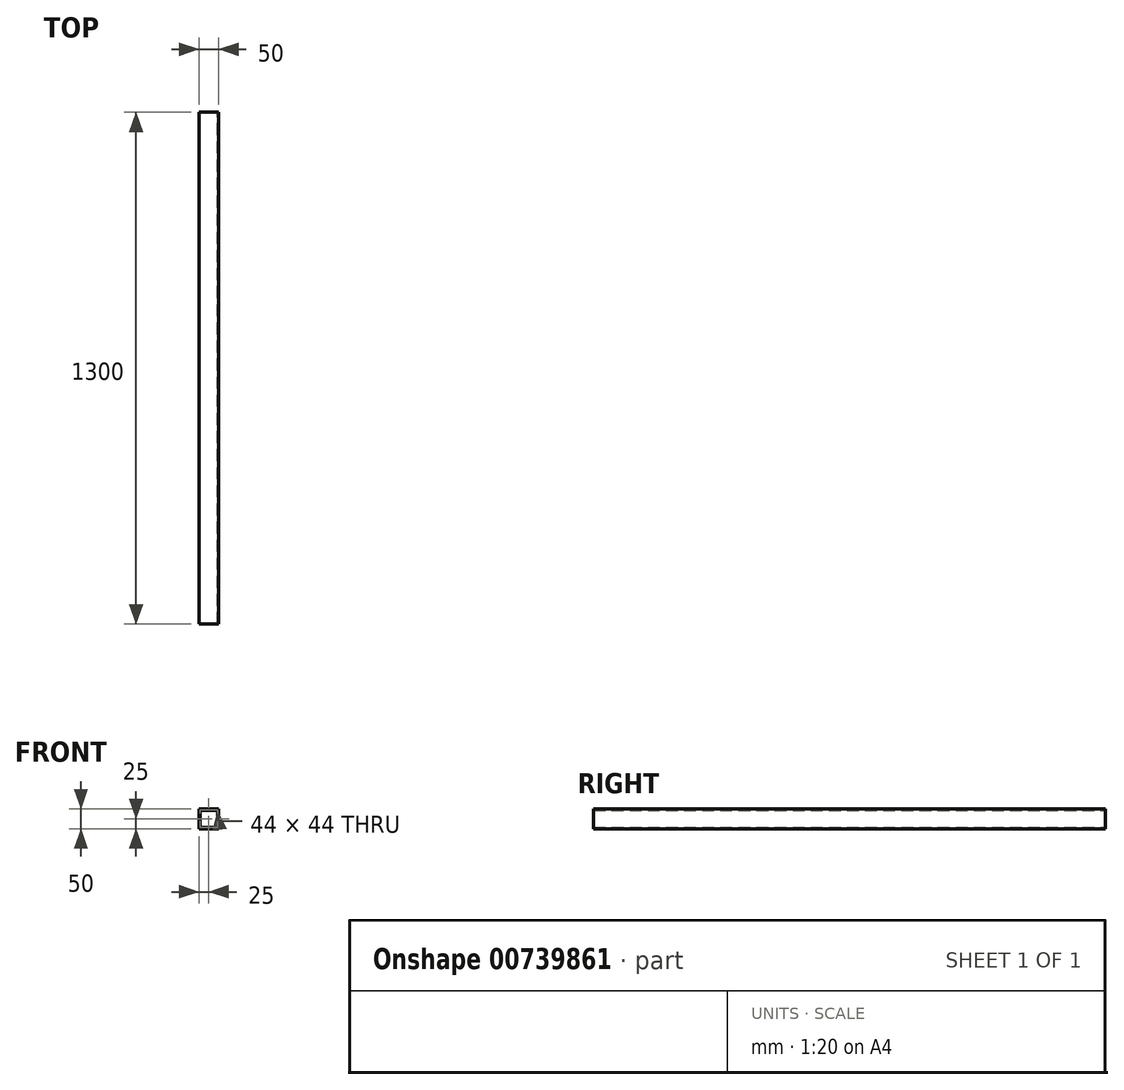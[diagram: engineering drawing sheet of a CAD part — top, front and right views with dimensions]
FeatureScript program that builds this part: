
annotation { "Feature Type Name" : "Feature", "Feature Type Description" : "" }
export const myFeature = defineFeature(function(context is Context, id is Id, definition is map)
    precondition{}
    {
        {
            var Q0;
            Q0=qCreatedBy(makeId("Front.planeOp"),FACE);
            var sketch = newSketch(context, id + "F0", { "sketchPlane" : qUnion([Q0])});
            skLineSegment(sketch, "E0.bottom", {"start": v(25, -25) * mm, "end": v(-25, -25) * mm});
            skLineSegment(sketch, "E0.top", {"start": v(25, 25) * mm, "end": v(-25, 25) * mm});
            skLineSegment(sketch, "E0.left", {"start": v(25, -25) * mm, "end": v(25, 25) * mm});
            skLineSegment(sketch, "E0.right", {"start": v(-25, -25) * mm, "end": v(-25, 25) * mm});
            skPoint(sketch, "E0.middle", {"position": v(0, 0) * mm});
            skLineSegment(sketch, "E1.0", {"start": v(22, 22) * mm, "end": v(-22, 22) * mm});
            skLineSegment(sketch, "E1.1", {"start": v(22, -22) * mm, "end": v(22, 22) * mm});
            skLineSegment(sketch, "E1.2", {"start": v(22, -22) * mm, "end": v(-22, -22) * mm});
            skLineSegment(sketch, "E1.3", {"start": v(-22, -22) * mm, "end": v(-22, 22) * mm});
            skSolve(sketch);
        }
        {
            var Q0;
            Q0 = qSketchRegion(id + "F0", true);
            extrude(context, id + "F1", {"entities" : qUnion([Q0]), "depth" : 1300 * mm, "offsetDistance" : 25 * mm});
        }
    });
